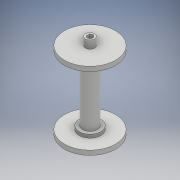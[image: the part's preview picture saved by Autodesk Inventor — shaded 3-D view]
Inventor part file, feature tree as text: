
AUTODESK INVENTOR PART (.ipt)
format: ipt  version: 2017 (Build 210142000, 142)  size: 181,760 bytes
history: native  units: mm
features: sketch x3, extrude x2, revolve x1
ambient origin geometry x8: Origin, YZ Plane, XZ Plane, XY Plane, X Axis, Y Axis, Z Axis, Center Point
bodies: Body1 (feature_tree)
feature tree (6):
  revolve  "Revolution2"  [1 undecoded]
  extrude  "Extrusion6"  Depth=7.0mm
  extrude  "Extrusion7"  Depth=4.0mm
  sketch  "Sketch1"  dims[d1=2.5mm d2=4.0mm]
  sketch  "Sketch6"  dims[d3=7.0mm d4=20.0mm]
  sketch  "Sketch7"  dims[d5=34.0mm d9=4.0mm d12=2.5mm d13=4.0mm d55=22.5mm d56=4.0mm d57=90.0deg d64=20.0mm d65=90.0deg d69=15.0mm d71=15.0mm d73=5.0mm d74=0.0mm d75=2.5mm d76=5.0mm d77=5.0mm d78=26.0mm d79=0.0mm d80=3.0mm d81=3.0mm d82=3.0mm d83=3.0mm]
note: 1 required parameter value undecoded (feature->parameter linkage not recoverable at this tier; creation-order binding heuristic only, values carry confidence <= 0.55)
